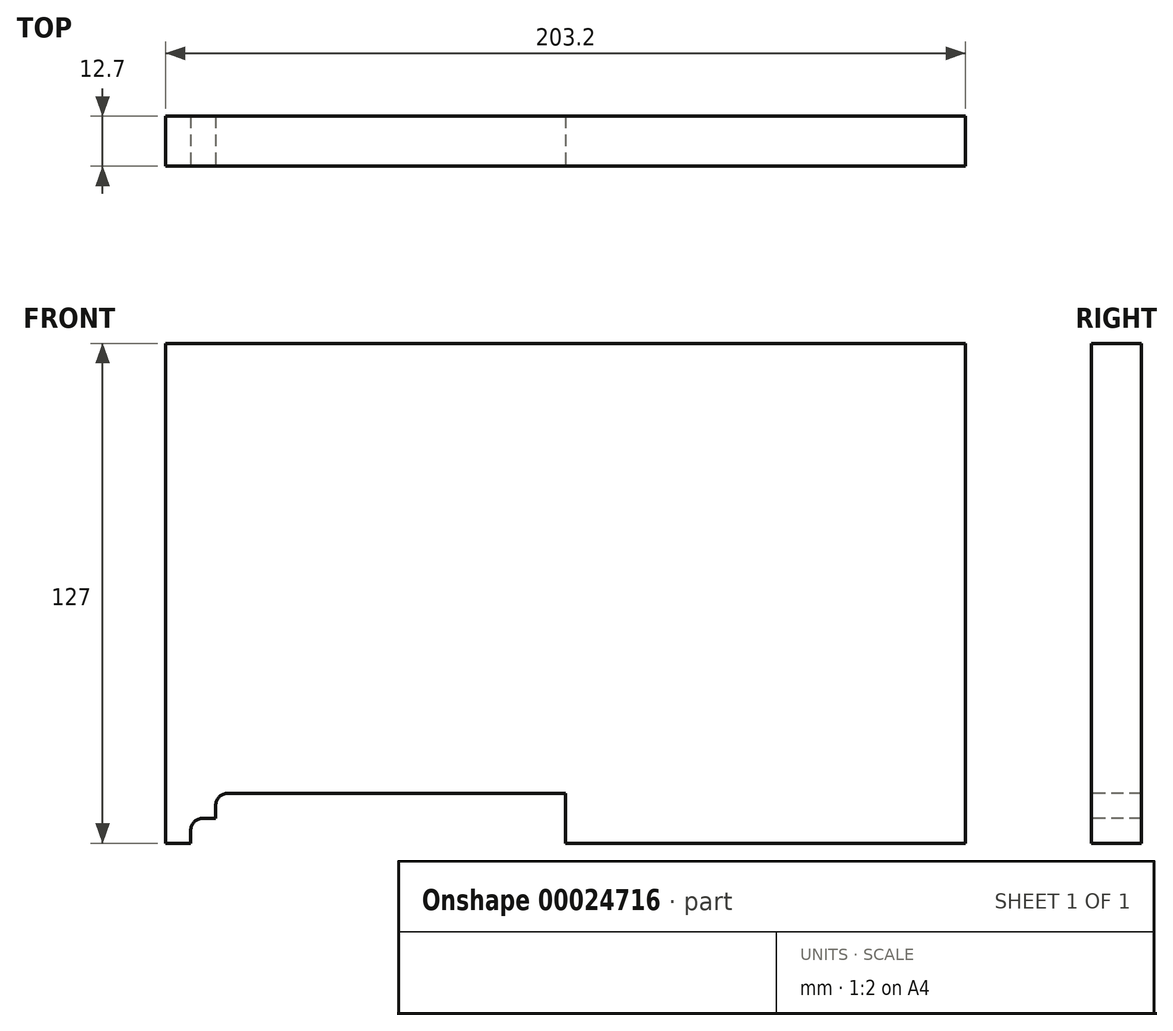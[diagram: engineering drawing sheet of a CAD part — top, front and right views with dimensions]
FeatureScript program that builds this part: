
annotation { "Feature Type Name" : "Feature", "Feature Type Description" : "" }
export const myFeature = defineFeature(function(context is Context, id is Id, definition is map)
    precondition{}
    {
        {
            var Q0;
            Q0=qCreatedBy(makeId("Front.planeOp"),FACE);
            var sketch = newSketch(context, id + "F0", { "sketchPlane" : qUnion([Q0])});
            skLineSegment(sketch, "E0.rect.bottom", {"start": v(-101.6, 63.5) * mm, "end": v(101.6, 63.5) * mm});
            skLineSegment(sketch, "E0.rect.top", {"start": v(-101.6, -63.5) * mm, "end": v(101.6, -63.5) * mm});
            skLineSegment(sketch, "E0.rect.left", {"start": v(-101.6, 63.5) * mm, "end": v(-101.6, -63.5) * mm});
            skLineSegment(sketch, "E0.rect.right", {"start": v(101.6, 63.5) * mm, "end": v(101.6, -63.5) * mm});
            skPoint(sketch, "E0.rect.middle", {"position": v(0, 0) * mm});
            skSolve(sketch);
        }
        {
            var Q0;
            Q0 = qSketchRegion(id + "F0", true);
            extrude(context, id + "F1", {"entities" : qUnion([Q0]), "depth" : 12.7 * mm});
        }
        {
            var Q0;
            Q0=makeQuery(id+"F1.opExtrude","CAP_FACE",FACE,{"disambiguationData":[OSD([sQuery(id+"F0.wireOp",EDGE,"E0.rect.bottom"),sQuery(id+"F0.wireOp",EDGE,"E0.rect.top"),sQuery(id+"F0.wireOp",EDGE,"E0.rect.left"),sQuery(id+"F0.wireOp",EDGE,"E0.rect.right")])],"isStart":false});
            var sketch = newSketch(context, id + "F2", { "sketchPlane" : qUnion([Q0])});
            skLineSegment(sketch, "E1", {"start": v(-95.25, -63.5) * mm, "end": v(-95.25, -60.32) * mm});
            skLineSegment(sketch, "E2", {"start": v(-92.08, -57.15) * mm, "end": v(-88.9, -57.15) * mm});
            skLineSegment(sketch, "E3", {"start": v(-88.9, -57.15) * mm, "end": v(-88.9, -53.97) * mm});
            skLineSegment(sketch, "E4", {"start": v(-85.73, -50.8) * mm, "end": v(0, -50.8) * mm});
            skLineSegment(sketch, "E5", {"start": v(0, -50.8) * mm, "end": v(0, -63.5) * mm});
            skLineSegment(sketch, "E6", {"start": v(0, -63.5) * mm, "end": v(-95.25, -63.5) * mm});
            skPoint(sketch, "E7.visualSharp", {"position": v(-95.25, -57.15) * mm});
            skArc(sketch, "E7.filletArc", {"start": v(-92.08, -57.15) * mm, "mid": v(-94.32, -58.08) * mm, "end": v(-95.25, -60.32) * mm});
            skPoint(sketch, "E8.visualSharp", {"position": v(-88.9, -50.8) * mm});
            skArc(sketch, "E8.filletArc", {"start": v(-85.73, -50.8) * mm, "mid": v(-87.97, -51.73) * mm, "end": v(-88.9, -53.97) * mm});
            skSolve(sketch);
        }
        {
            var Q0;
            Q0=makeQuery(id+"F2.imprint","IMPRINT",FACE,{"disambiguationData":[TD([[makeQuery(id+"F2.imprint","IMPRINT",EDGE,{"derivedFrom":sQuery(id+"F2.wireOp",EDGE,"E1")}),-1.0]])]});
            var Q1;
            Q1=sQuery(id+"F2.wireOp",EDGE,"E4");
            var Q2;
            Q2=sQuery(id+"F2.wireOp",EDGE,"E5");
            extrude(context, id + "F3", {"entities" : qUnion([Q0]), "operationType" : NewBodyOperationType.REMOVE, "surfaceEntities" : qUnion([Q1, Q2]), "endBound" : BoundingType.THROUGH_ALL, "oppositeDirection" : true, "depth" : 25.4 * mm});
        }
    });
